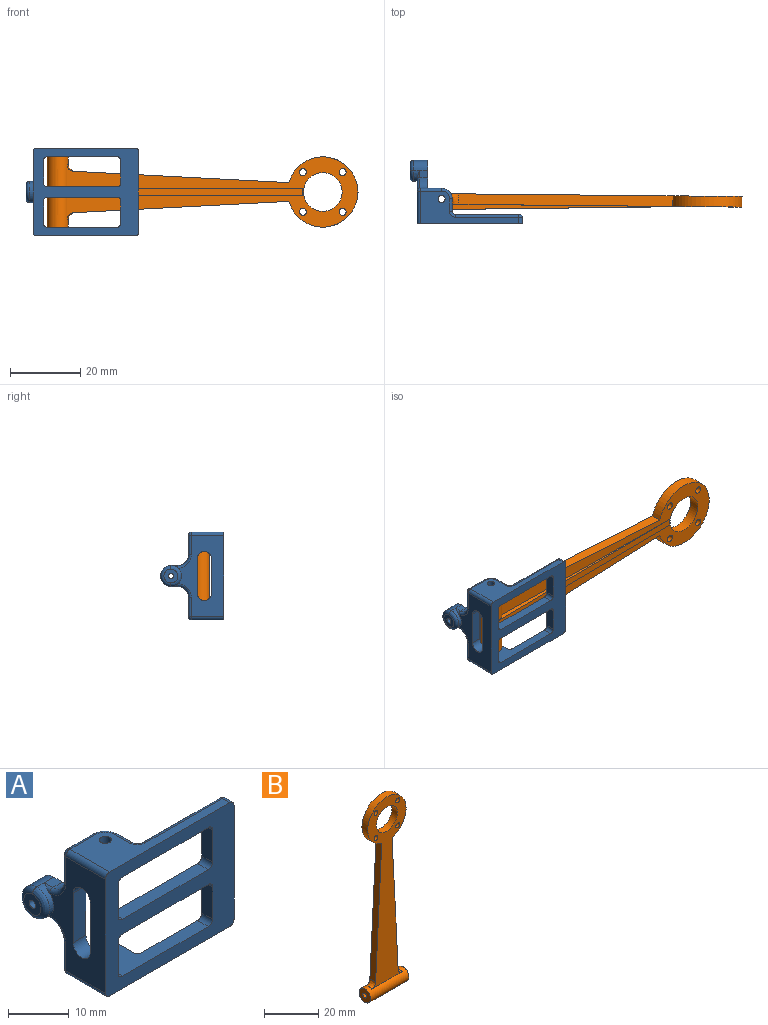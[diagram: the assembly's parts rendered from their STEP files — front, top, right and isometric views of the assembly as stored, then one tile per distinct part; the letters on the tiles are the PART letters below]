
ASSEMBLY  parts=2 mates=1
PART A: 71 faces, bbox 32x18.2x25 mm
  f0: plane 6.5x2.5mm, normal (-1,0,0), area 16.3mm2, adj f11,f12,f26,f42
  f1: plane 18x18mm, normal (1,0,0), area 156.2mm2, adj f3,f8,f12,f18,f19,f20,f21,f22
  f2: plane 23x13.02mm, normal (-1,0,0), area 180mm2, adj f12,f30,f32,f33,f46,f47,f48,f49
  f3: plane 6.25x5.75mm, normal (0,1,0), area 20.1mm2, adj f1,f7,f17,f22,f28,f52,f53,f54
  f4: plane 3.5x1.75mm, normal (1,0,0), area 6.1mm2, adj f6,f16,f45,f64
  f5: plane 3.5x1.75mm, normal (1,0,0), area 6.1mm2, adj f7,f17,f44,f56
  f6: cylinder r=3mm len=3mm, axis (0,0,-1), area 8.2mm2, adj f4,f8,f16,f65
  f7: cylinder r=3mm len=3mm, axis (0,0,-1), area 8.2mm2, adj f3,f5,f17,f55
  f8: plane 6.25x5.75mm, normal (0,1,0), area 20.1mm2, adj f1,f6,f16,f23,f27,f66,f67,f68
  f9: cylinder r=1mm len=2.5mm, axis (0,0,-1), area 15.7mm2, adj f14,f16
  f10: cylinder r=1mm len=2.5mm, axis (0,0,-1), area 15.7mm2, adj f15,f17
  f11: plane 25.25x23.5mm, normal (0,1,0), area 212.7mm2, adj f0,f16,f17,f24,f25,f26,f37,f38
  f12: plane 30x25mm, normal (0,-1,0), area 376.9mm2, adj f0,f1,f2,f13,f14,f15,f16,f17
  f13: plane 23x1.75mm, normal (1,0,0), area 40.2mm2, adj f12,f29,f31,f60
  f14: plane 28x9.25mm, normal (0,0,1), area 107.3mm2, adj f9,f12,f31,f32,f62,f63,f64,f65
  f15: plane 28x9.25mm, normal (0,0,-1), area 107.3mm2, adj f10,f12,f29,f30,f54,f55,f56,f57
  f16: plane 20x10mm, normal (0,0,-1), area 90.1mm2, adj f4,f6,f8,f9,f11,f12,f25,f27
  f17: plane 20x10mm, normal (0,0,1), area 90.1mm2, adj f3,f5,f7,f10,f11,f12,f26,f28
  f18: plane 2.25x2mm, normal (0,0,-1), area 4.5mm2, adj f1,f20,f22,f50
  f19: plane 2.25x2mm, normal (0,0,1), area 4.5mm2, adj f1,f20,f23,f70
  f20: cylinder r=3mm len=6mm, axis (-1,0,0), area 38.5mm2, adj f1,f18,f19,f33,f36,f50
  f21: cylinder r=0.75mm len=5mm, axis (-1,0,0), area 23.6mm2, adj f1,f34
  f22: cylinder r=3mm len=3mm, axis (-1,0,0), area 10.6mm2, adj f1,f3,f18,f51
  f23: cylinder r=3mm len=3mm, axis (1,0,0), area 10.6mm2, adj f1,f8,f19,f69
  f24: plane 6.5x2.5mm, normal (-1,0,0), area 16.3mm2, adj f11,f12,f25,f43
  f25: cylinder r=1mm len=2.5mm, axis (0,1,0), area 3.9mm2, adj f11,f12,f16,f24
  f26: cylinder r=1mm len=2.5mm, axis (0,1,0), area 3.9mm2, adj f0,f11,f12,f17
  f27: cylinder r=1mm len=10mm, axis (0,-1,0), area 15.7mm2, adj f1,f8,f12,f16
  f28: cylinder r=1mm len=10mm, axis (0,-1,0), area 15.7mm2, adj f1,f3,f12,f17
  f29: cylinder r=1mm len=1.75mm, axis (0,1,0), area 2.7mm2, adj f12,f13,f15,f59
  f30: cylinder r=1mm len=9.25mm, axis (0,-1,0), area 14.5mm2, adj f2,f12,f15,f53
  f31: cylinder r=1mm len=1.75mm, axis (0,-1,0), area 2.7mm2, adj f12,f13,f14,f61
  f32: cylinder r=1mm len=9.25mm, axis (0,1,0), area 14.5mm2, adj f2,f12,f14,f67
  f33: extruded ~6x3mm, area 10.2mm2, adj f2,f20,f35,f70
  f34: plane 4x4mm, normal (-1,0,0), area 10.8mm2, adj f21,f35,f36
  f35: bspline ~6x5.7mm, area 13mm2, adj f33,f34,f36
  f36: torus R=2mm, axis (-1,0,0), area 13mm2, adj f20,f34,f35
  f37: plane 20x2.5mm, normal (0,0,-1), area 50mm2, adj f11,f12,f39,f42
  f38: plane 20x2.5mm, normal (0,0,1), area 50mm2, adj f11,f12,f40,f43
  f39: cylinder r=1mm len=3.5mm, axis (0,1,0), area 4.7mm2, adj f1,f12,f37,f41
  f40: cylinder r=1mm len=3.5mm, axis (0,1,0), area 4.7mm2, adj f1,f12,f38,f41
  f41: cylinder r=1mm len=5mm, axis (0,0,-1), area 6.3mm2, adj f11,f39,f40,f46
  f42: cylinder r=1mm len=2.5mm, axis (0,-1,0), area 3.9mm2, adj f0,f11,f12,f37
  f43: cylinder r=1mm len=2.5mm, axis (0,-1,0), area 3.9mm2, adj f11,f12,f24,f38
  f44: cylinder r=1mm len=1.75mm, axis (0,0,1), area 2.7mm2, adj f5,f11,f17,f57
  f45: cylinder r=1mm len=1.75mm, axis (0,0,1), area 2.7mm2, adj f4,f11,f16,f63
  f46: plane 10x3mm, normal (0,1,0), area 30mm2, adj f1,f2,f41,f47,f49
  f47: cylinder r=2mm len=4mm, axis (1,0,0), area 18.8mm2, adj f1,f2,f46,f48
  f48: plane 10x3mm, normal (0,-1,0), area 30mm2, adj f1,f2,f47,f49
  f49: cylinder r=2mm len=4mm, axis (1,0,0), area 18.8mm2, adj f1,f2,f46,f48
  f50: cylinder r=0.75mm len=2mm, axis (0,-1,0), area 1.1mm2, adj f2,f18,f20,f51
  f51: torus R=3.75mm, axis (-1,0,0), area 6.1mm2, adj f2,f22,f50,f52
  f52: cylinder r=0.75mm len=5.5mm, axis (0,0,-1), area 6.5mm2, adj f2,f3,f51,f53
  f53: torus R=0.25mm, axis (0,1,0), area 1.3mm2, adj f3,f30,f52,f54
  f54: cylinder r=0.75mm len=6mm, axis (-1,0,0), area 7.1mm2, adj f3,f15,f53,f55
  f55: torus R=2.25mm, axis (0,0,1), area 5mm2, adj f7,f15,f54,f56
  f56: cylinder r=0.75mm len=3.5mm, axis (0,1,0), area 4.1mm2, adj f5,f15,f55,f57
  f57: torus R=1.75mm, axis (0,0,1), area 2.4mm2, adj f15,f44,f56,f58
  f58: cylinder r=0.75mm len=18mm, axis (-1,0,0), area 21.2mm2, adj f11,f15,f57,f59
  f59: torus R=0.25mm, axis (0,1,0), area 1.3mm2, adj f11,f29,f58,f60
  f60: cylinder r=0.75mm len=23mm, axis (0,0,-1), area 27.1mm2, adj f11,f13,f59,f61
  f61: torus R=0.25mm, axis (0,1,0), area 1.3mm2, adj f11,f31,f60,f62
  f62: cylinder r=0.75mm len=18mm, axis (1,0,0), area 21.2mm2, adj f11,f14,f61,f63
  f63: torus R=1.75mm, axis (0,0,1), area 2.4mm2, adj f14,f45,f62,f64
  f64: cylinder r=0.75mm len=3.5mm, axis (0,-1,0), area 4.1mm2, adj f4,f14,f63,f65
  f65: torus R=2.25mm, axis (0,0,1), area 5mm2, adj f6,f14,f64,f66
  f66: cylinder r=0.75mm len=6mm, axis (1,0,0), area 7.1mm2, adj f8,f14,f65,f67
  f67: torus R=0.25mm, axis (0,1,0), area 1.3mm2, adj f8,f32,f66,f68
  f68: cylinder r=0.75mm len=5.5mm, axis (0,0,-1), area 6.5mm2, adj f2,f8,f67,f69
  f69: torus R=3.75mm, axis (-1,0,0), area 6.1mm2, adj f2,f23,f68,f70
  f70: cylinder r=0.75mm len=2mm, axis (0,1,0), area 1.1mm2, adj f2,f19,f33,f69
PART B: 19 faces, bbox 20.2x6.2x88.7 mm
  f0: cylinder r=3mm len=20mm, axis (-1,0,0), area 321.4mm2, adj f1,f2,f11,f12,f14,f15,f16,f17
  f1: plane 83.07x20.17mm, normal (0,-1,0), area 755.7mm2, adj f0,f3,f4,f5,f6,f7,f8,f9
  f2: plane 83.07x20.17mm, normal (0,1,0), area 621.3mm2, adj f0,f3,f4,f5,f6,f7,f8,f9
  f3: plane 61.2x3.21mm, normal (1,0,0.05), area 183.4mm2, adj f1,f2,f4,f14
  f4: cylinder r=10mm len=20mm, axis (0,1,0), area 172.2mm2, adj f1,f2,f3,f5
  f5: plane 61.2x3.21mm, normal (-1,0,0.05), area 183.4mm2, adj f1,f2,f4,f15
  f6: cylinder r=1mm len=3mm, axis (0,1,0), area 18.8mm2, adj f1,f2
  f7: cylinder r=1mm len=3mm, axis (0,1,0), area 18.8mm2, adj f1,f2
  f8: cylinder r=1mm len=3mm, axis (0,1,0), area 18.8mm2, adj f1,f2
  f9: cylinder r=5.5mm len=11mm, axis (0,1,0), area 103.7mm2, adj f1,f2
  f10: cylinder r=1mm len=3mm, axis (0,1,0), area 18.8mm2, adj f1,f2
  f11: plane 6x6mm, normal (-1,0,0), area 25.1mm2, adj f0,f13
  f12: plane 6x6mm, normal (1,0,0), area 25.1mm2, adj f0,f13
  f13: cylinder r=1mm len=20mm, axis (1,0,0), area 125.7mm2, adj f11,f12
  f14: bspline ~5x2.3mm, area 9.2mm2, adj f0,f1,f2,f3
  f15: bspline ~5x2.3mm, area 9.2mm2, adj f0,f1,f2,f5
  f16: plane 69.71x2mm, normal (0,1,0.02), area 139.4mm2, adj f0,f2,f17,f18
  f17: plane 69.71x1.5mm, normal (1,0,0), area 49.6mm2, adj f0,f2,f16
  f18: plane 69.71x1.5mm, normal (-1,0,0), area 49.6mm2, adj f0,f2,f16
PLACE A t=(-21.12,4.82,-1.54)mm fixed
PLACE B rot(axis=(0.71,0,0.71),179.6deg) t=(-16.64,10.35,10.96)mm
MATE revolute A.f6 <-> B.f0  axis (0,0,1) through (-14.12,11.82,0.96)mm
